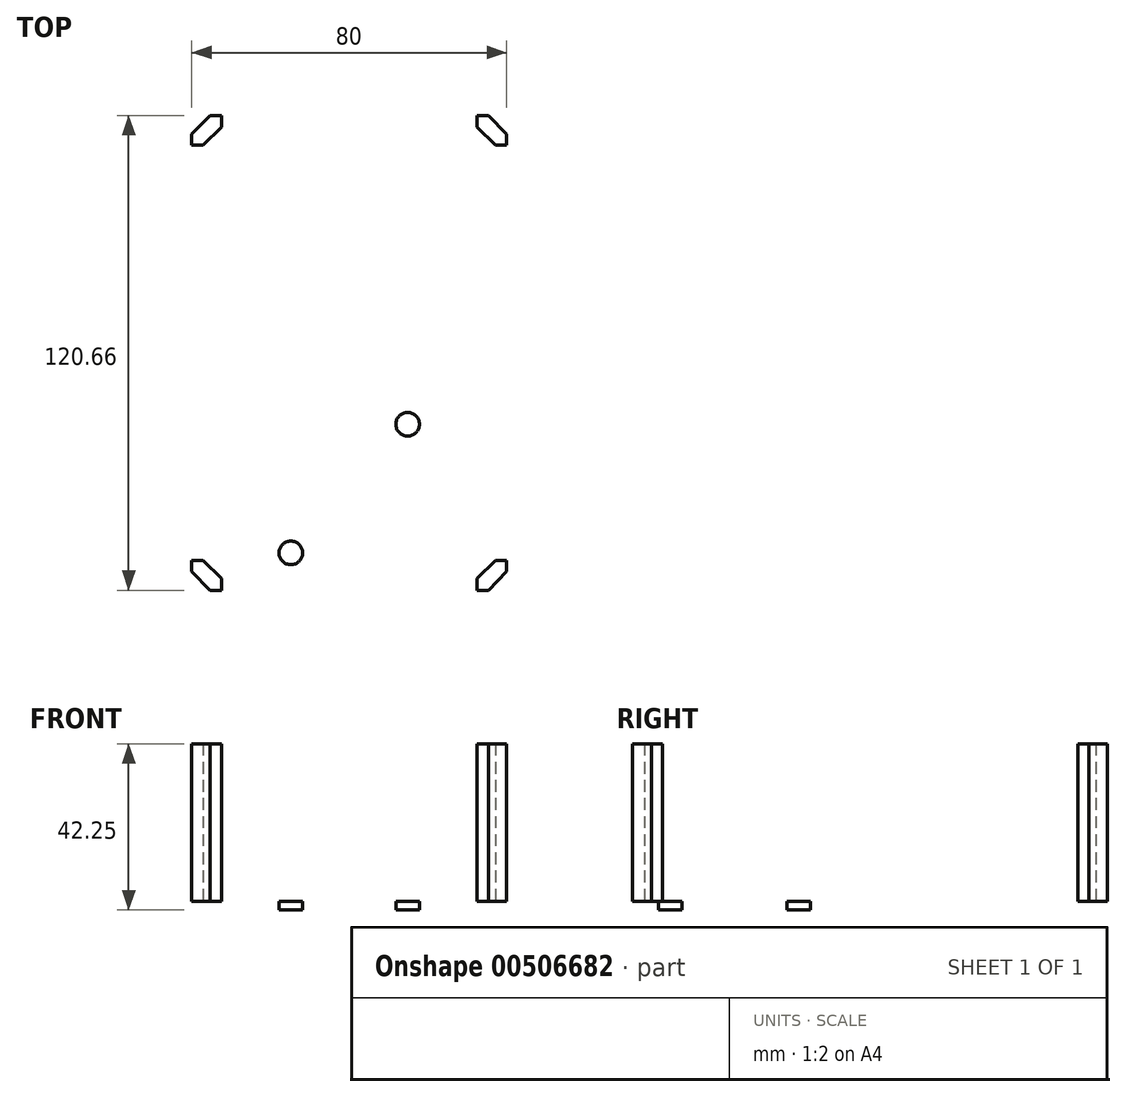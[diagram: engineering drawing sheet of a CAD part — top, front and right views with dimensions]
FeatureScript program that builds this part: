
annotation { "Feature Type Name" : "Feature", "Feature Type Description" : "" }
export const myFeature = defineFeature(function(context is Context, id is Id, definition is map)
    precondition{}
    {
        {
            var Q0;
            Q0=qCreatedBy(makeId("Top.planeOp"),FACE);
            var sketch = newSketch(context, id + "F0", { "sketchPlane" : qUnion([Q0])});
            skLineSegment(sketch, "E0.rect.bottom", {"start": v(-40, -60.33) * mm, "end": v(40, -60.33) * mm});
            skLineSegment(sketch, "E0.rect.top", {"start": v(-40, 60.33) * mm, "end": v(40, 60.33) * mm});
            skLineSegment(sketch, "E0.rect.left", {"start": v(-40, -60.33) * mm, "end": v(-40, 60.33) * mm});
            skLineSegment(sketch, "E0.rect.right", {"start": v(40, -60.33) * mm, "end": v(40, 60.33) * mm});
            skPoint(sketch, "E0.rect.middle", {"position": v(0, 0) * mm});
            skLineSegment(sketch, "E1", {"start": v(-35.41, 60.33) * mm, "end": v(-40, 55.6) * mm});
            skLineSegment(sketch, "E2", {"start": v(-35.22, -60.32) * mm, "end": v(-40, -55.8) * mm});
            skLineSegment(sketch, "E3.0.MirrorCS", {"start": v(35.22, -60.32) * mm, "end": v(40, -55.8) * mm});
            skLineSegment(sketch, "E4.0.MirrorCS", {"start": v(35.41, 60.33) * mm, "end": v(40, 55.6) * mm});
            skSolve(sketch);
        }
        {
            var Q0;
            {var subQ3=sQuery(id+"F0.wireOp",EDGE,"E1");Q0=makeQuery(id+"F0.imprint","IMPRINT",FACE,{"disambiguationData":[TD([[makeQuery(id+"F0.imprint","IMPRINT",EDGE,{"derivedFrom":subQ3}),1.0]])]});}
            extrude(context, id + "F1", {"entities" : qUnion([Q0]), "depth" : 2.25 * mm});
        }
        {
            var Q0;
            Q0=makeQuery(id+"F1.opExtrude","CAP_FACE",FACE,{"disambiguationData":[OSD([sQuery(id+"F0.wireOp",EDGE,"E0.rect.bottom"),sQuery(id+"F0.wireOp",EDGE,"E0.rect.top"),sQuery(id+"F0.wireOp",EDGE,"E0.rect.left"),sQuery(id+"F0.wireOp",EDGE,"E0.rect.right")])],"isStart":false});
            var sketch = newSketch(context, id + "F2", { "sketchPlane" : qUnion([Q0])});
            skCircle(sketch, "E5", {"center": v(-25, -34.48) * mm, "radius": 14.29 * mm, "construction": true});
            skCircle(sketch, "E6", {"center": v(-25, -34.48) * mm, "radius": 5.5 * mm});
            skCircle(sketch, "E7", {"center": v(-19.3, -16.1) * mm, "radius": 3 * mm});
            skCircle(sketch, "E8.0.MirrorC", {"center": v(-14.84, -50.82) * mm, "radius": 3 * mm});
            skLineSegment(sketch, "E9", {"start": v(-14.84, -50.82) * mm, "end": v(-19.3, -16.1) * mm, "construction": true});
            skLineSegment(sketch, "E10", {"start": v(-25, -34.48) * mm, "end": v(-17.07, -33.46) * mm, "construction": true});
            skCircle(sketch, "E11.1.0", {"center": v(25, -34.48) * mm, "radius": 5.5 * mm});
            skCircle(sketch, "E11.1.1", {"center": v(14.84, -18.14) * mm, "radius": 3 * mm});
            skCircle(sketch, "E11.1.2", {"center": v(19.3, -52.85) * mm, "radius": 3 * mm});
            skPoint(sketch, "E11.center", {"position": v(0, -34.48) * mm});
            skSolve(sketch);
        }
        {
            var Q0;
            Q0=makeQuery(id+"F2.imprint","IMPRINT",FACE,{"disambiguationData":[TD([[makeQuery(id+"F2.imprint","IMPRINT",EDGE,{"derivedFrom":sQuery(id+"F2.wireOp",EDGE,"E6")}),1.0]])]});
            var Q1;
            Q1=makeQuery(id+"F2.imprint","IMPRINT",FACE,{"disambiguationData":[TD([[makeQuery(id+"F2.imprint","IMPRINT",EDGE,{"derivedFrom":sQuery(id+"F2.wireOp",EDGE,"E7")}),1.0]])]});
            var Q2;
            Q2=makeQuery(id+"F2.imprint","IMPRINT",FACE,{"disambiguationData":[TD([[makeQuery(id+"F2.imprint","IMPRINT",EDGE,{"derivedFrom":sQuery(id+"F2.wireOp",EDGE,"E8.0.MirrorC")}),-1.0]])]});
            var Q3;
            Q3=makeQuery(id+"F2.imprint","IMPRINT",FACE,{"disambiguationData":[TD([[makeQuery(id+"F2.imprint","IMPRINT",EDGE,{"derivedFrom":sQuery(id+"F2.wireOp",EDGE,"E11.1.0")}),1.0]])]});
            var Q4;
            Q4=makeQuery(id+"F2.imprint","IMPRINT",FACE,{"disambiguationData":[TD([[makeQuery(id+"F2.imprint","IMPRINT",EDGE,{"derivedFrom":sQuery(id+"F2.wireOp",EDGE,"E11.1.2")}),1.0]])]});
            var Q5;
            Q5=makeQuery(id+"F2.imprint","IMPRINT",FACE,{"disambiguationData":[TD([[makeQuery(id+"F2.imprint","IMPRINT",EDGE,{"derivedFrom":sQuery(id+"F2.wireOp",EDGE,"E11.1.1")}),-1.0]])]});
            extrude(context, id + "F3", {"entities" : qUnion([Q0, Q1, Q2, Q3, Q4, Q5]), "operationType" : NewBodyOperationType.REMOVE, "oppositeDirection" : true, "depth" : 25.4 * mm});
        }
        {
            var Q0;
            Q0=makeQuery(id+"F1.opExtrude","CAP_FACE",FACE,{"disambiguationData":[OSD([sQuery(id+"F0.wireOp",EDGE,"E0.rect.bottom"),sQuery(id+"F0.wireOp",EDGE,"E0.rect.top"),sQuery(id+"F0.wireOp",EDGE,"E0.rect.left"),sQuery(id+"F0.wireOp",EDGE,"E0.rect.right")])],"isStart":true});
            var sketch = newSketch(context, id + "F4", { "sketchPlane" : qUnion([Q0])});
            skText(sketch, "E12", { "text": "HUGBOT", "fontName": "OpenSans-Bold.ttf"});
            const initialGuessF4  = {"E12": [-0.03225, -0.05059, 1, 0, 0.01068]};
            skSetInitialGuess(sketch, initialGuessF4);
            skSolve(sketch);
        }
        {
            var Q0;
            Q0=makeQuery(id+"F4.imprint","IMPRINT",FACE,{"disambiguationData":[TD([[makeQuery(id+"F4.imprint","IMPRINT",EDGE,{"derivedFrom":sQuery(id+"F4.wireOp",EDGE,"E12.sketch_text.stroke-71")}),-1.0]])]});
            var Q1;
            Q1=makeQuery(id+"F4.imprint","IMPRINT",FACE,{"disambiguationData":[TD([[makeQuery(id+"F4.imprint","IMPRINT",EDGE,{"derivedFrom":sQuery(id+"F4.wireOp",EDGE,"E12.sketch_text.stroke-85")}),-1.0]])]});
            var Q2;
            Q2=makeQuery(id+"F4.imprint","IMPRINT",FACE,{"disambiguationData":[TD([[makeQuery(id+"F4.imprint","IMPRINT",EDGE,{"derivedFrom":sQuery(id+"F4.wireOp",EDGE,"E12.sketch_text.stroke-46")}),-1.0]])]});
            var Q3;
            Q3=makeQuery(id+"F4.imprint","IMPRINT",FACE,{"disambiguationData":[TD([[makeQuery(id+"F4.imprint","IMPRINT",EDGE,{"derivedFrom":sQuery(id+"F4.wireOp",EDGE,"E12.sketch_text.stroke-27")}),-1.0]])]});
            var Q4;
            Q4=makeQuery(id+"F4.imprint","IMPRINT",FACE,{"disambiguationData":[TD([[makeQuery(id+"F4.imprint","IMPRINT",EDGE,{"derivedFrom":sQuery(id+"F4.wireOp",EDGE,"E12.sketch_text.stroke-12")}),-1.0]])]});
            var Q5;
            Q5=makeQuery(id+"F4.imprint","IMPRINT",FACE,{"disambiguationData":[TD([[makeQuery(id+"F4.imprint","IMPRINT",EDGE,{"derivedFrom":sQuery(id+"F4.wireOp",EDGE,"E12.sketch_text.stroke-0")}),-1.0]])]});
            extrude(context, id + "F5", {"entities" : qUnion([Q0, Q1, Q2, Q3, Q4, Q5]), "operationType" : NewBodyOperationType.REMOVE, "oppositeDirection" : true, "depth" : .3 * mm});
        }
        {
            var Q0;
            Q0=makeQuery(id+"F1.opExtrude","CAP_FACE",FACE,{"disambiguationData":[OSD([sQuery(id+"F0.wireOp",EDGE,"E0.rect.bottom"),sQuery(id+"F0.wireOp",EDGE,"E0.rect.top"),sQuery(id+"F0.wireOp",EDGE,"E0.rect.left"),sQuery(id+"F0.wireOp",EDGE,"E0.rect.right"),sQuery(id+"F0.wireOp",EDGE,"E1"),sQuery(id+"F0.wireOp",EDGE,"E2")])],"isStart":false});
            var sketch = newSketch(context, id + "F6", { "sketchPlane" : qUnion([Q0])});
            skLineSegment(sketch, "E13", {"start": v(-32.45, 60.33) * mm, "end": v(-32.45, 57.36) * mm});
            skLineSegment(sketch, "E14", {"start": v(-32.45, 57.36) * mm, "end": v(-37.17, 52.78) * mm});
            skLineSegment(sketch, "E15", {"start": v(-37.17, 52.78) * mm, "end": v(-40, 52.78) * mm});
            skLineSegment(sketch, "E16", {"start": v(-32.45, 60.33) * mm, "end": v(-35.41, 60.33) * mm});
            skLineSegment(sketch, "E17", {"start": v(-40, 55.6) * mm, "end": v(-35.41, 60.33) * mm});
            skLineSegment(sketch, "E18", {"start": v(-40, 52.78) * mm, "end": v(-40, 55.6) * mm});
            skLineSegment(sketch, "E19.0.MirrorCS", {"start": v(32.45, 60.33) * mm, "end": v(35.41, 60.33) * mm});
            skLineSegment(sketch, "E20.0.MirrorCS", {"start": v(32.45, 57.36) * mm, "end": v(37.17, 52.78) * mm});
            skLineSegment(sketch, "E21.0.MirrorCS", {"start": v(37.17, 52.78) * mm, "end": v(40, 52.78) * mm});
            skLineSegment(sketch, "E22.0.MirrorCS", {"start": v(32.45, 60.33) * mm, "end": v(32.45, 57.36) * mm});
            skLineSegment(sketch, "E23.0.MirrorCS", {"start": v(40, 55.6) * mm, "end": v(35.41, 60.33) * mm});
            skLineSegment(sketch, "E24.0.MirrorCS", {"start": v(40, 52.78) * mm, "end": v(40, 55.6) * mm});
            skLineSegment(sketch, "E25.0.MirrorCS", {"start": v(-40, -52.78) * mm, "end": v(-40, -55.6) * mm});
            skLineSegment(sketch, "E25.1.MirrorCS", {"start": v(-32.45, -60.33) * mm, "end": v(-35.41, -60.33) * mm});
            skLineSegment(sketch, "E25.2.MirrorCS", {"start": v(-40, -55.6) * mm, "end": v(-35.41, -60.33) * mm});
            skLineSegment(sketch, "E25.3.MirrorCS", {"start": v(-32.45, -57.36) * mm, "end": v(-37.17, -52.78) * mm});
            skLineSegment(sketch, "E26.0.MirrorCS", {"start": v(-37.17, -52.78) * mm, "end": v(-40, -52.78) * mm});
            skLineSegment(sketch, "E26.4.MirrorCS", {"start": v(-32.45, -60.33) * mm, "end": v(-32.45, -57.36) * mm});
            skLineSegment(sketch, "E27.0.MirrorCS", {"start": v(32.45, -60.33) * mm, "end": v(32.45, -57.36) * mm});
            skLineSegment(sketch, "E27.1.MirrorCS", {"start": v(40, -55.6) * mm, "end": v(35.41, -60.33) * mm});
            skLineSegment(sketch, "E27.2.MirrorCS", {"start": v(32.45, -60.33) * mm, "end": v(35.41, -60.33) * mm});
            skLineSegment(sketch, "E27.3.MirrorCS", {"start": v(40, -52.78) * mm, "end": v(40, -55.6) * mm});
            skLineSegment(sketch, "E27.4.MirrorCS", {"start": v(37.17, -52.78) * mm, "end": v(40, -52.78) * mm});
            skLineSegment(sketch, "E27.5.MirrorCS", {"start": v(32.45, -57.36) * mm, "end": v(37.17, -52.78) * mm});
            skSolve(sketch);
        }
        {
            var Q0;
            Q0=qSketchRegion(id+"F6",true);
            extrude(context, id + "F7", {"entities" : qUnion([Q0]), "operationType" : NewBodyOperationType.ADD, "depth" : 40 * mm});
        }
    });
